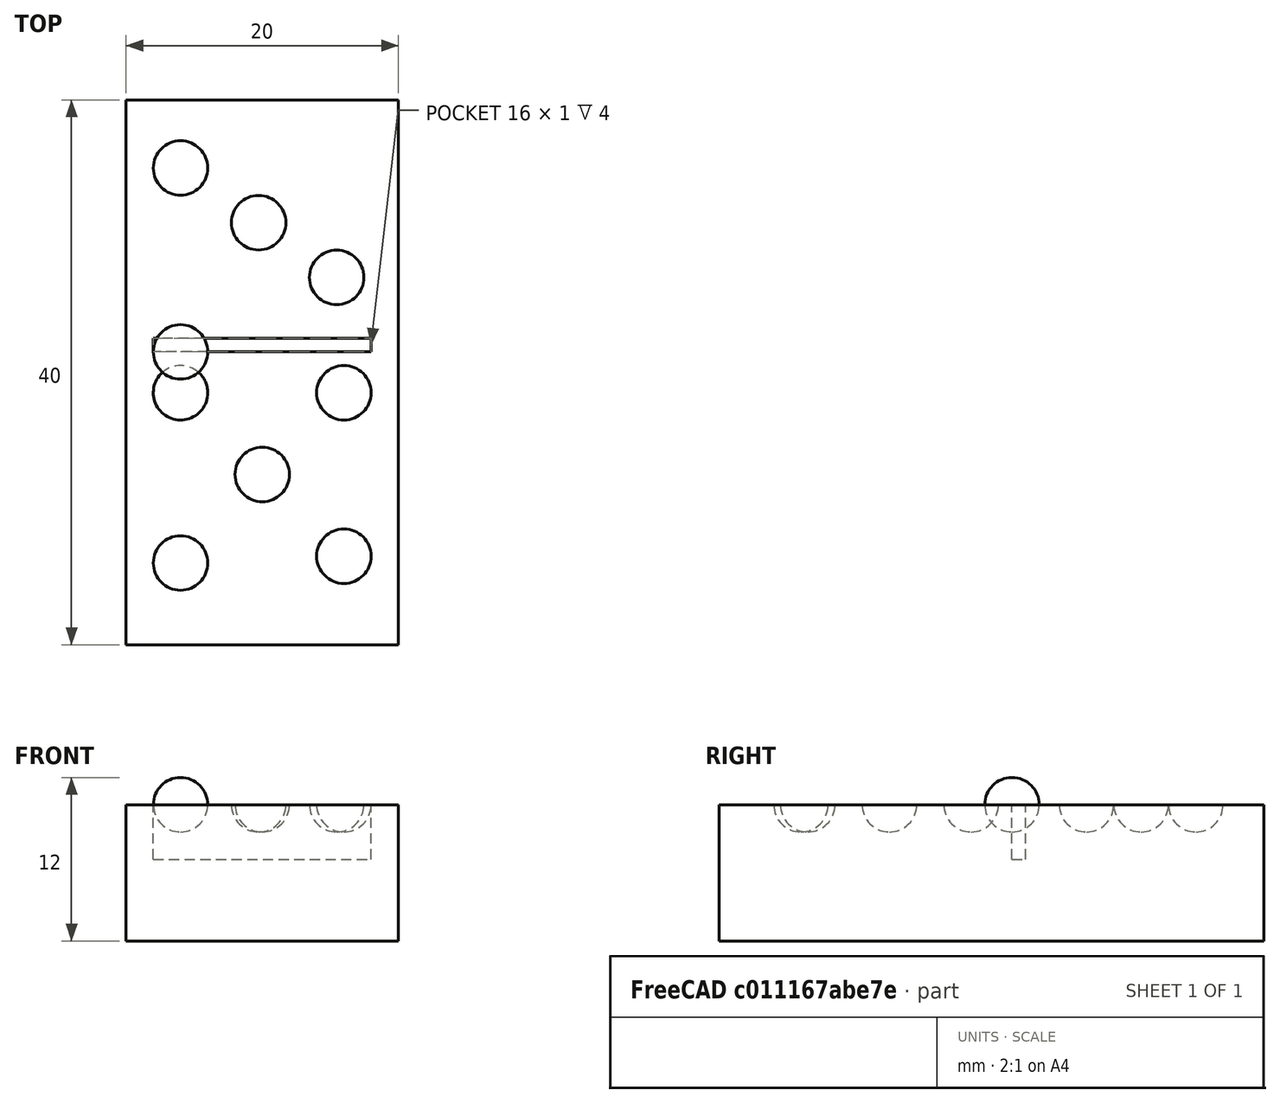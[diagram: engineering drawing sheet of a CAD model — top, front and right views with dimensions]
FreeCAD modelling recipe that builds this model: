
FCSTD DOCUMENT  (FreeCAD 1.0R39319 (Git))
Label: ojt1_t13r03_dado
License: All rights reserved
LicenseURL: https://en.wikipedia.org/wiki/All_rights_reserved
objects: Part::FeaturePython×7, Part::Cut×3, Part::Sphere×2, Part::Box×2, Part::MultiFuse×1, App::DocumentObjectGroup×1
note: 13 computed .brp shape members not serialized (recipe doc carries the construction recipe); baked Part::Feature solids carry a one-line shape summary decoded from their .brp

FEATURE [Part::Sphere] Sphere001  label="Esfera001"
  Angle1 = -90
  Angle2 = 90
  Angle3 = 360
  AttacherType = Attacher::AttachEngine3D
  Radius = 2
FEATURE [Part::FeaturePython] Array001  # Draft array (typed FeaturePython)
  AlwaysSyncPlacement = false
  Angle = 360
  ArrayType = 0
  Axis = (0,0,1)
  Base = -> Sphere001
  Center = (0,0,0)
  Count = 9
  ExpandArray = false
  Fuse = false
  IntervalAxis = (0,0,0)
  IntervalX = (6,2,0)
  IntervalY = (0,6,0)
  IntervalZ = (0,0,100)
  NumberCircles = 3
  NumberPolar = 5
  NumberX = 3
  NumberY = 3
  NumberZ = 1
  Placement = pos=(0,-19,0) rot=(0,0,1;0rad)
  PlacementList = 9 placements: [(0,0,0),(0,6,0),(0,12,0),(6,2,0),(6,8,0),(6,14,0),(12,4,0),(12,10,0),(12,16,0)]
  RadialDistance = 50
  ScaleList = (9) [(1,1,1),(1,1,1),(1,1,1),(1,1,1),(1,1,1),(1,1,1),(1,1,1),(1,1,1),(1,1,1)]
  Symmetry = 1
  TangentialDistance = 25
FEATURE [Part::FeaturePython] Array001_child0  label="Array001.0"  # WARN: FeaturePython — macro-defined, semantics opaque (R4)
  Base = -> Array001
  FilterType = 1
  Invert = false
  OverrideMaxVal = 0
  Placement = pos=(0,3.5,0) rot=(0,0,1;0rad)
  WindowFrom = 80
  WindowTo = 100
  items = 0
FEATURE [Part::FeaturePython] Array001_child2  label="Array001.2"  # WARN: FeaturePython — macro-defined, semantics opaque (R4)
  Base = -> Array001
  FilterType = 1
  Invert = false
  OverrideMaxVal = 0
  Placement = pos=(0,4,0) rot=(0,0,1;0rad)
  WindowFrom = 80
  WindowTo = 100
  items = 2
FEATURE [Part::FeaturePython] Array001_child4  label="Array001.4"  # WARN: FeaturePython — macro-defined, semantics opaque (R4)
  Base = -> Array001
  FilterType = 1
  Invert = false
  OverrideMaxVal = 0
  Placement = pos=(0,2,0) rot=(0,0,1;0rad)
  WindowFrom = 80
  WindowTo = 100
  items = 4
FEATURE [Part::FeaturePython] Array001_child6  label="Array001.6"  # WARN: FeaturePython — macro-defined, semantics opaque (R4)
  Base = -> Array001
  FilterType = 1
  Invert = false
  OverrideMaxVal = 0
  WindowFrom = 80
  WindowTo = 100
  items = 6
FEATURE [Part::FeaturePython] Array001_child8  label="Array001.8"  # WARN: FeaturePython — macro-defined, semantics opaque (R4)
  Base = -> Array001
  FilterType = 1
  Invert = false
  OverrideMaxVal = 0
  WindowFrom = 80
  WindowTo = 100
  items = 8
FEATURE [Part::Box] Box  label="Cub"
  AttacherType = Attacher::AttachEngine3D
  Height = 10
  Length = 20
  Placement = pos=(-4,-21.5,-10) rot=(0,0,1;0rad)
  Width = 40
FEATURE [Part::Box] Box001  label="Cub001"
  AttacherType = Attacher::AttachEngine3D
  Height = 10
  Length = 16
  Placement = pos=(-2,0,-4) rot=(0,0,1;0rad)
  Width = 1
FEATURE [Part::Cut] Cut
  Base = -> Box
  Refine = true
  Tool = -> Box001
FEATURE [Part::MultiFuse] Fusion
  Refine = true
  Shapes = -> [Array001_child8,Array001_child6,Array001_child4,Array001_child2,Array001_child0]
FEATURE [Part::Cut] Cut001
  Base = -> Cut
  Refine = true
  Tool = -> Fusion
FEATURE [Part::Sphere] Sphere  label="Esfera"
  Angle1 = -90
  Angle2 = 90
  Angle3 = 360
  AttacherType = Attacher::AttachEngine3D
  Radius = 2
FEATURE [Part::FeaturePython] Array  # Draft array (typed FeaturePython)
  AlwaysSyncPlacement = false
  Angle = 360
  ArrayType = 0
  Axis = (0,0,1)
  Base = -> Sphere
  Center = (0,0,0)
  Count = 3
  ExpandArray = false
  Fuse = false
  IntervalAxis = (0,0,0)
  IntervalX = (7,0,0)
  IntervalY = (0,0,0)
  IntervalZ = (0,0,100)
  NumberCircles = 3
  NumberPolar = 5
  NumberX = 3
  NumberY = 1
  NumberZ = 1
  Placement = pos=(0,13.5,0) rot=(0,0,-1;0.610865rad)
  PlacementList = 3 placements: arithmetic series from (0,0,0) step (7,0,0) to (14,0,0)
  RadialDistance = 50
  ScaleList = (3) [(1,1,1),(1,1,1),(1,1,1)]
  Symmetry = 1
  TangentialDistance = 25
FEATURE [Part::Cut] Cut002
  Base = -> Cut001
  Refine = true
  Tool = -> Array
FEATURE [App::DocumentObjectGroup] GrExplode_Array001  label="Exploded Array001"
  Group = -> [Cut002]
